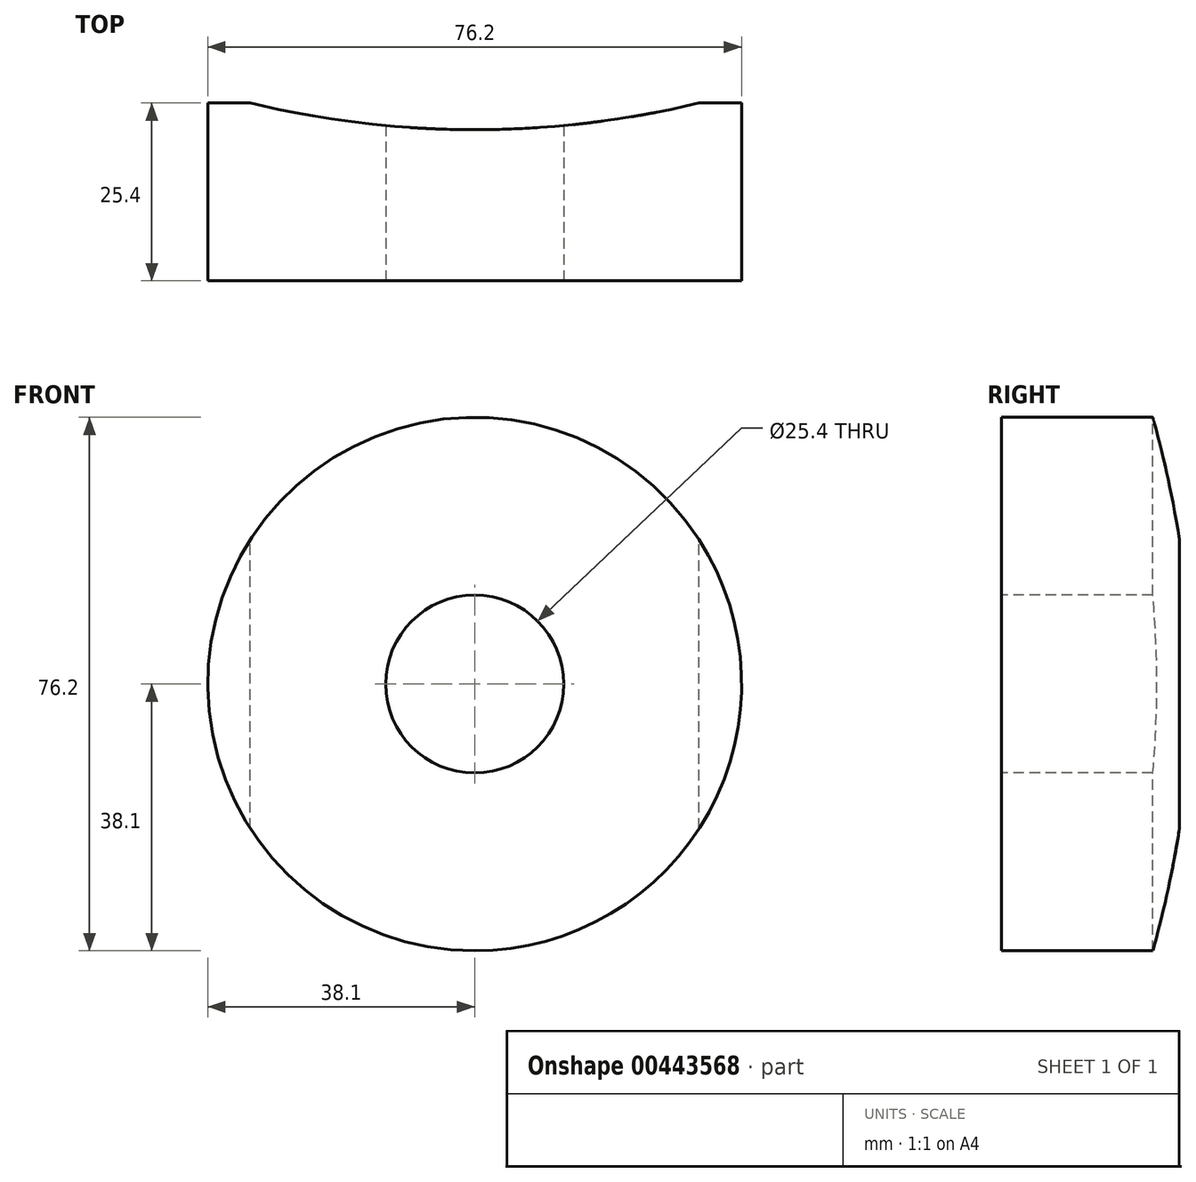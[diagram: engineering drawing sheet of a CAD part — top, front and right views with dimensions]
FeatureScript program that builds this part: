
annotation { "Feature Type Name" : "Feature", "Feature Type Description" : "" }
export const myFeature = defineFeature(function(context is Context, id is Id, definition is map)
    precondition{}
    {
        {
            var Q0;
            Q0=qCreatedBy(makeId("Front.planeOp"),FACE);
            var sketch = newSketch(context, id + "F0", { "sketchPlane" : qUnion([Q0])});
            skCircle(sketch, "E0", {"center": v(0, 0) * mm, "radius": 38.1 * mm});
            skSolve(sketch);
        }
        {
            var Q0;
            Q0 = qSketchRegion(id + "F0", true);
            extrude(context, id + "F1", {"entities" : qUnion([Q0]), "depth" : 25.4 * mm});
        }
        {
            var Q0;
            Q0=makeQuery(id+"F1.opExtrude","CAP_FACE",FACE,{"disambiguationData":[OSD([sQuery(id+"F0.wireOp",EDGE,"E0")])],"isStart":false});
            var sketch = newSketch(context, id + "F2", { "sketchPlane" : qUnion([Q0])});
            skCircle(sketch, "E1", {"center": v(0, 0) * mm, "radius": 12.7 * mm});
            skSolve(sketch);
        }
        {
            var Q0;
            Q0 = qSketchRegion(id + "F2", true);
            extrude(context, id + "F3", {"entities" : qUnion([Q0]), "operationType" : NewBodyOperationType.REMOVE, "endBound" : BoundingType.THROUGH_ALL, "oppositeDirection" : true, "depth" : 12.7 * mm});
        }
        {
            var Q0;
            Q0=qCreatedBy(makeId("Top.planeOp"),FACE);
            var sketch = newSketch(context, id + "F4", { "sketchPlane" : qUnion([Q0])});
            skArc(sketch, "E2", {"start": v(-32.03, 0) * mm, "mid": v(0, -3.81) * mm, "end": v(32.03, 0) * mm});
            skLineSegment(sketch, "E3", {"start": v(0, 132.72) * mm, "end": v(0, 0) * mm, "construction": true});
            skLineSegment(sketch, "E4.0", {"start": v(32.03, 0) * mm, "end": v(-32.03, 0) * mm});
            skSolve(sketch);
        }
        {
            var Q0;
            Q0 = qSketchRegion(id + "F4", true);
            extrude(context, id + "F5", {"entities" : qUnion([Q0]), "operationType" : NewBodyOperationType.REMOVE, "endBound" : BoundingType.THROUGH_ALL, "oppositeDirection" : true, "depth" : 25.4 * mm, "hasSecondDirection" : true, "secondDirectionBound" : BoundingType.THROUGH_ALL, "secondDirectionOppositeDirection" : false, "secondDirectionDepth" : 25.4 * mm});
        }
    });
